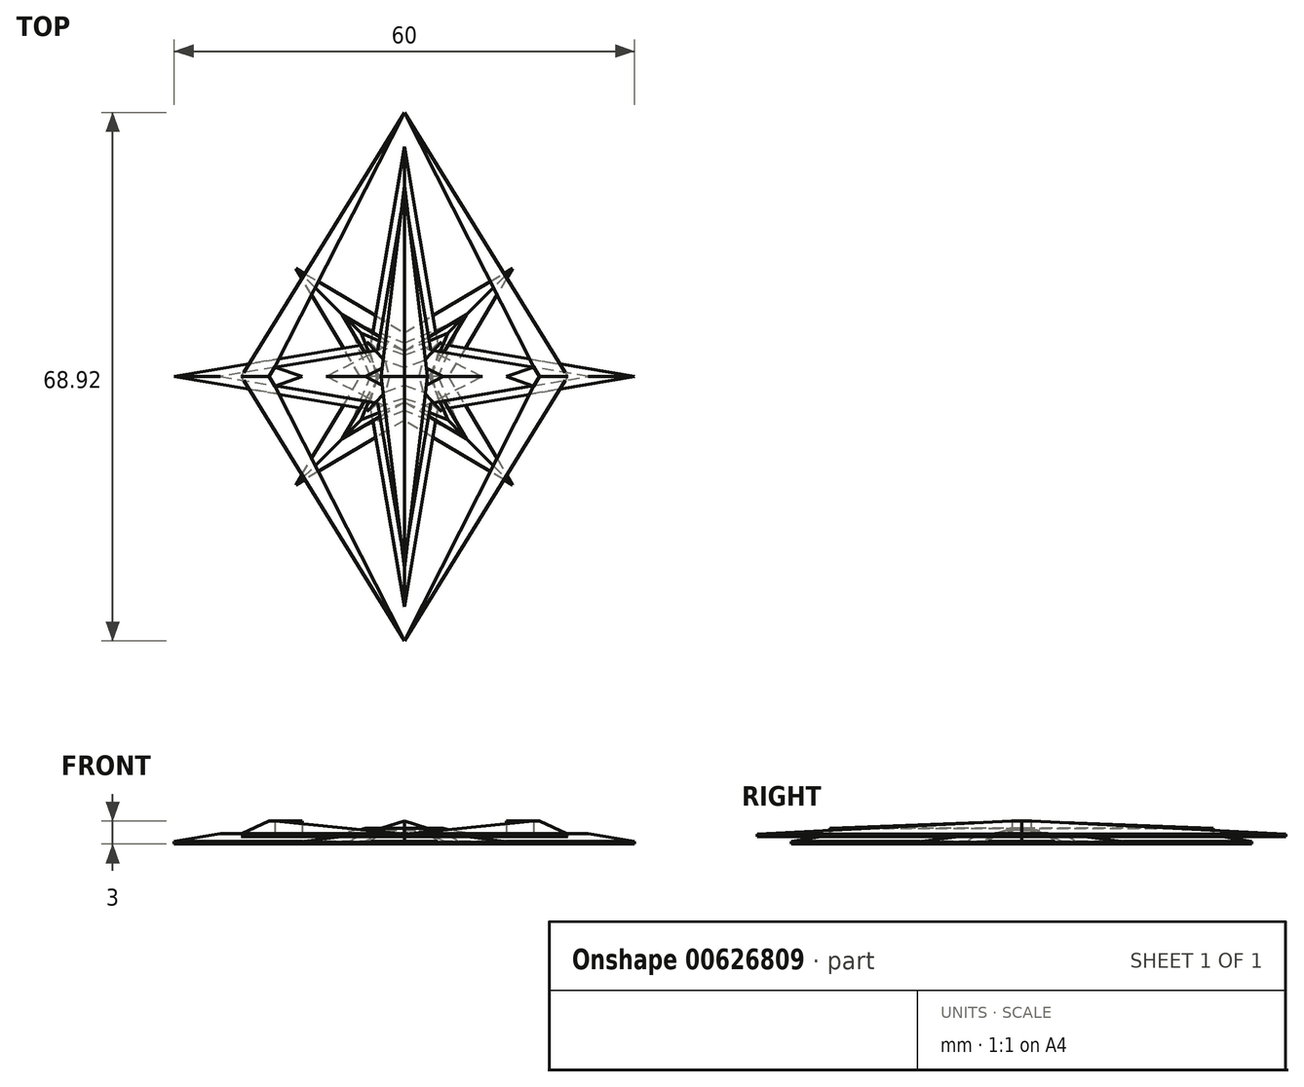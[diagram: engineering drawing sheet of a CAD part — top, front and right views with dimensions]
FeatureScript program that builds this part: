
annotation { "Feature Type Name" : "Feature", "Feature Type Description" : "" }
export const myFeature = defineFeature(function(context is Context, id is Id, definition is map)
    precondition{}
    {
        {
            var Q0;
            Q0=qCreatedBy(makeId("Top.planeOp"),FACE);
            var sketch = newSketch(context, id + "F0", { "sketchPlane" : qUnion([Q0])});
            skLineSegment(sketch, "E0", {"start": v(0, 0) * mm, "end": v(0, 50) * mm});
            skLineSegment(sketch, "E1", {"start": v(0, 25) * mm, "end": v(10.5, 25) * mm});
            skPoint(sketch, "E1.endSnap0", {"position": v(0, 25) * mm});
            skLineSegment(sketch, "E2.MirrorCS", {"start": v(0, 25) * mm, "end": v(-10.5, 25) * mm});
            skLineSegment(sketch, "E3", {"start": v(-10.5, 25) * mm, "end": v(0, 30.33) * mm});
            skLineSegment(sketch, "E4.MirrorCS", {"start": v(-10.5, 25) * mm, "end": v(0, 19.67) * mm});
            skLineSegment(sketch, "E5.MirrorCS", {"start": v(10.5, 25) * mm, "end": v(0, 30.33) * mm});
            skLineSegment(sketch, "E6.MirrorCS", {"start": v(10.5, 25) * mm, "end": v(0, 19.67) * mm});
            skLineSegment(sketch, "E7", {"start": v(0, 50) * mm, "end": v(-3, 25) * mm});
            skLineSegment(sketch, "E8.MirrorCS", {"start": v(0, 50) * mm, "end": v(3, 25) * mm});
            skLineSegment(sketch, "E9.MirrorCS", {"start": v(0, 0) * mm, "end": v(-3, 25) * mm});
            skLineSegment(sketch, "E10.MirrorCS", {"start": v(0, 0) * mm, "end": v(3, 25) * mm});
            skLineSegment(sketch, "E11", {"start": v(5.42, 30.16) * mm, "end": v(0, 28.23) * mm});
            skLineSegment(sketch, "E12.MirrorCS", {"start": v(5.42, 30.16) * mm, "end": v(3.97, 25) * mm});
            skLineSegment(sketch, "E13.MirrorCS", {"start": v(-5.42, 30.16) * mm, "end": v(0, 28.23) * mm});
            skLineSegment(sketch, "E14.MirrorCS", {"start": v(-5.42, 30.16) * mm, "end": v(-3.97, 25) * mm});
            skLineSegment(sketch, "E15.MirrorCS", {"start": v(5.42, 19.84) * mm, "end": v(0, 21.77) * mm});
            skLineSegment(sketch, "E16.MirrorCS", {"start": v(5.42, 19.84) * mm, "end": v(3.97, 25) * mm});
            skLineSegment(sketch, "E17.MirrorCS", {"start": v(-5.42, 19.84) * mm, "end": v(0, 21.77) * mm});
            skLineSegment(sketch, "E18.MirrorCS", {"start": v(-5.42, 19.84) * mm, "end": v(-3.97, 25) * mm});
            skLineSegment(sketch, "E19", {"start": v(0, -9.46) * mm, "end": v(-16.87, 23.77) * mm});
            skLineSegment(sketch, "E20.MirrorCS", {"start": v(0, 59.46) * mm, "end": v(-16.87, 26.23) * mm});
            skLineSegment(sketch, "E21.MirrorCS", {"start": v(0, 59.46) * mm, "end": v(16.87, 26.23) * mm});
            skLineSegment(sketch, "E22.MirrorCS", {"start": v(0, -9.46) * mm, "end": v(16.87, 23.77) * mm});
            skLineSegment(sketch, "E23", {"start": v(0, 59.46) * mm, "end": v(-21.27, 25) * mm});
            skPoint(sketch, "E23.endSnap0", {"position": v(-5.25, 25) * mm});
            skLineSegment(sketch, "E24.MirrorCS", {"start": v(0, -9.46) * mm, "end": v(-21.27, 25) * mm});
            skLineSegment(sketch, "E25.MirrorCS", {"start": v(0, 59.46) * mm, "end": v(21.27, 25) * mm});
            skLineSegment(sketch, "E26.MirrorCS", {"start": v(0, -9.46) * mm, "end": v(21.27, 25) * mm});
            skLineSegment(sketch, "E27", {"start": v(-13.32, 25) * mm, "end": v(-16.87, 26.23) * mm});
            skLineSegment(sketch, "E28.MirrorCS", {"start": v(-13.32, 25) * mm, "end": v(-16.87, 23.77) * mm});
            skLineSegment(sketch, "E29.MirrorCS", {"start": v(13.32, 25) * mm, "end": v(16.87, 26.23) * mm});
            skLineSegment(sketch, "E30.MirrorCS", {"start": v(13.32, 25) * mm, "end": v(16.87, 23.77) * mm});
            skPoint(sketch, "E31.orphan", {"position": v(-17.5, 25) * mm});
            skPoint(sketch, "E32.orphan", {"position": v(17.5, 25) * mm});
            skSolve(sketch);
        }
        {
            var Q0;
            Q0=qCreatedBy(makeId("Top.planeOp"),FACE);
            var sketch = newSketch(context, id + "F1", { "sketchPlane" : qUnion([Q0])});
            skLineSegment(sketch, "E33", {"start": v(0, 0) * mm, "end": v(0, 25) * mm});
            skLineSegment(sketch, "E34", {"start": v(0, 25) * mm, "end": v(0, 55) * mm});
            skLineSegment(sketch, "E35", {"start": v(0, 25) * mm, "end": v(30, 25) * mm});
            skLineSegment(sketch, "E36", {"start": v(0, 25) * mm, "end": v(-30, 25) * mm});
            skLineSegment(sketch, "E37", {"start": v(0, 25) * mm, "end": v(0, -5) * mm});
            skLineSegment(sketch, "E38", {"start": v(0, 55) * mm, "end": v(-4.33, 29.33) * mm});
            skLineSegment(sketch, "E39", {"start": v(-4.33, 29.33) * mm, "end": v(-30, 25) * mm});
            skLineSegment(sketch, "E40.MirrorCS", {"start": v(0, 55) * mm, "end": v(4.33, 29.33) * mm});
            skLineSegment(sketch, "E41.MirrorCS", {"start": v(4.33, 29.33) * mm, "end": v(30, 25) * mm});
            skLineSegment(sketch, "E42.MirrorCS", {"start": v(-4.33, 20.67) * mm, "end": v(-30, 25) * mm});
            skLineSegment(sketch, "E43.MirrorCS", {"start": v(0, -5) * mm, "end": v(-4.33, 20.67) * mm});
            skLineSegment(sketch, "E44.MirrorCS", {"start": v(0, -5) * mm, "end": v(4.33, 20.67) * mm});
            skLineSegment(sketch, "E45.MirrorCS", {"start": v(4.33, 20.67) * mm, "end": v(30, 25) * mm});
            skLineSegment(sketch, "E46", {"start": v(0, 25) * mm, "end": v(-7.48, 32.48) * mm});
            skLineSegment(sketch, "E47.MirrorCS", {"start": v(0, 25) * mm, "end": v(7.48, 32.48) * mm});
            skLineSegment(sketch, "E48.MirrorCS", {"start": v(0, 25) * mm, "end": v(-7.48, 17.52) * mm});
            skLineSegment(sketch, "E49.MirrorCS", {"start": v(0, 25) * mm, "end": v(7.48, 17.52) * mm});
            skLineSegment(sketch, "E50", {"start": v(-7.48, 32.48) * mm, "end": v(-4.41, 25) * mm});
            skLineSegment(sketch, "E51.MirrorCS", {"start": v(-7.48, 32.48) * mm, "end": v(0, 29.41) * mm});
            skLineSegment(sketch, "E52.MirrorCS", {"start": v(7.48, 32.48) * mm, "end": v(0, 29.41) * mm});
            skLineSegment(sketch, "E53.MirrorCS", {"start": v(7.48, 32.48) * mm, "end": v(4.41, 25) * mm});
            skLineSegment(sketch, "E54.MirrorCS", {"start": v(-7.48, 17.52) * mm, "end": v(0, 20.59) * mm});
            skLineSegment(sketch, "E55.MirrorCS", {"start": v(-7.48, 17.52) * mm, "end": v(-4.41, 25) * mm});
            skLineSegment(sketch, "E56.MirrorCS", {"start": v(7.48, 17.52) * mm, "end": v(0, 20.59) * mm});
            skLineSegment(sketch, "E57.MirrorCS", {"start": v(7.48, 17.52) * mm, "end": v(4.41, 25) * mm});
            skSolve(sketch);
        }
        {
            var Q0;
            Q0=qCreatedBy(makeId("Top.planeOp"),FACE);
            var sketch = newSketch(context, id + "F2", { "sketchPlane" : qUnion([Q0])});
            skLineSegment(sketch, "E58", {"start": v(0, 0) * mm, "end": v(0, 25) * mm});
            skLineSegment(sketch, "E59", {"start": v(0, 25) * mm, "end": v(25, 25) * mm});
            skLineSegment(sketch, "E60", {"start": v(0, 25) * mm, "end": v(14.14, 10.86) * mm});
            skLineSegment(sketch, "E61.MirrorCS", {"start": v(0, 25) * mm, "end": v(14.14, 39.14) * mm});
            skLineSegment(sketch, "E62.MirrorCS", {"start": v(0, 25) * mm, "end": v(-14.14, 39.14) * mm});
            skLineSegment(sketch, "E63.MirrorCS", {"start": v(0, 25) * mm, "end": v(-14.14, 10.86) * mm});
            skLineSegment(sketch, "E64", {"start": v(-14.14, 39.14) * mm, "end": v(-5.72, 25) * mm});
            skLineSegment(sketch, "E65", {"start": v(-5.72, 25) * mm, "end": v(-14.14, 10.86) * mm});
            skPoint(sketch, "E66", {"position": v(-5.72, 25) * mm});
            skPoint(sketch, "E67.MirrorP", {"position": v(0, 30.72) * mm});
            skPoint(sketch, "E68.MirrorP", {"position": v(5.72, 25) * mm});
            skPoint(sketch, "E69.MirrorP", {"position": v(0, 19.28) * mm});
            skLineSegment(sketch, "E70", {"start": v(-14.14, 10.86) * mm, "end": v(0, 19.28) * mm});
            skLineSegment(sketch, "E71", {"start": v(14.14, 10.86) * mm, "end": v(0, 19.28) * mm});
            skLineSegment(sketch, "E72", {"start": v(14.14, 10.86) * mm, "end": v(5.72, 25) * mm});
            skLineSegment(sketch, "E73", {"start": v(5.72, 25) * mm, "end": v(14.14, 39.14) * mm});
            skLineSegment(sketch, "E74", {"start": v(14.14, 39.14) * mm, "end": v(0, 30.72) * mm});
            skLineSegment(sketch, "E75", {"start": v(0, 30.72) * mm, "end": v(-14.14, 39.14) * mm});
            skSolve(sketch);
        }
        {
            var Q0;
            {var subQ3=sQuery(id+"F0.wireOp",EDGE,"E3");var subQ5=sQuery(id+"F0.wireOp",EDGE,"E7");var subQ7=makeQuery(id+"F0.imprint","INTERSECT",VERTEX,{"derivedFrom":[subQ3,subQ5]});Q0=makeQuery(id+"F0.imprint","IMPRINT",FACE,{"disambiguationData":[TD([[makeQuery(id+"F0.imprint","IMPRINT",EDGE,{"disambiguationData":[TD([[subQ7,-1.0]])],"derivedFrom":subQ3}),-1.0]])]});}
            var Q1;
            {var subQ3=sQuery(id+"F0.wireOp",EDGE,"E4.MirrorCS");var subQ5=sQuery(id+"F0.wireOp",EDGE,"E9.MirrorCS");var subQ7=makeQuery(id+"F0.imprint","INTERSECT",VERTEX,{"derivedFrom":[subQ3,subQ5]});Q1=makeQuery(id+"F0.imprint","IMPRINT",FACE,{"disambiguationData":[TD([[makeQuery(id+"F0.imprint","IMPRINT",EDGE,{"disambiguationData":[TD([[subQ7,-1.0]])],"derivedFrom":subQ3}),1.0]])]});}
            var Q2;
            {var subQ3=sQuery(id+"F0.wireOp",EDGE,"E5.MirrorCS");var subQ5=sQuery(id+"F0.wireOp",EDGE,"E8.MirrorCS");var subQ7=makeQuery(id+"F0.imprint","INTERSECT",VERTEX,{"derivedFrom":[subQ3,subQ5]});Q2=makeQuery(id+"F0.imprint","IMPRINT",FACE,{"disambiguationData":[TD([[makeQuery(id+"F0.imprint","IMPRINT",EDGE,{"disambiguationData":[TD([[subQ7,-1.0]])],"derivedFrom":subQ3}),1.0]])]});}
            var Q3;
            {var subQ3=sQuery(id+"F0.wireOp",EDGE,"E6.MirrorCS");var subQ5=sQuery(id+"F0.wireOp",EDGE,"E10.MirrorCS");var subQ7=makeQuery(id+"F0.imprint","INTERSECT",VERTEX,{"derivedFrom":[subQ3,subQ5]});Q3=makeQuery(id+"F0.imprint","IMPRINT",FACE,{"disambiguationData":[TD([[makeQuery(id+"F0.imprint","IMPRINT",EDGE,{"disambiguationData":[TD([[subQ7,-1.0]])],"derivedFrom":subQ3}),-1.0]])]});}
            var Q4;
            {var subQ0=sQuery(id+"F0.wireOp",EDGE,"E8.MirrorCS");var subQ5=makeQuery(id+"F0.imprint","INTERSECT",VERTEX,{"derivedFrom":[subQ0,sQuery(id+"F0.wireOp",EDGE,"E11")]});Q4=makeQuery(id+"F0.imprint","IMPRINT",FACE,{"disambiguationData":[TD([[makeQuery(id+"F0.imprint","IMPRINT",EDGE,{"disambiguationData":[TD([[subQ5,-1.0]])],"derivedFrom":subQ0}),-1.0]])]});}
            var Q5;
            {var subQ0=sQuery(id+"F0.wireOp",EDGE,"E7");var subQ6=makeQuery(id+"F0.imprint","INTERSECT",VERTEX,{"derivedFrom":[subQ0,sQuery(id+"F0.wireOp",EDGE,"E13.MirrorCS")]});Q5=makeQuery(id+"F0.imprint","IMPRINT",FACE,{"disambiguationData":[TD([[makeQuery(id+"F0.imprint","IMPRINT",EDGE,{"disambiguationData":[TD([[subQ6,-1.0]])],"derivedFrom":subQ0}),1.0]])]});}
            var Q6;
            {var subQ0=sQuery(id+"F0.wireOp",EDGE,"E9.MirrorCS");var subQ6=makeQuery(id+"F0.imprint","INTERSECT",VERTEX,{"derivedFrom":[subQ0,sQuery(id+"F0.wireOp",EDGE,"E17.MirrorCS")]});Q6=makeQuery(id+"F0.imprint","IMPRINT",FACE,{"disambiguationData":[TD([[makeQuery(id+"F0.imprint","IMPRINT",EDGE,{"disambiguationData":[TD([[subQ6,-1.0]])],"derivedFrom":subQ0}),-1.0]])]});}
            var Q7;
            {var subQ0=sQuery(id+"F0.wireOp",EDGE,"E10.MirrorCS");var subQ5=makeQuery(id+"F0.imprint","INTERSECT",VERTEX,{"derivedFrom":[subQ0,sQuery(id+"F0.wireOp",EDGE,"E15.MirrorCS")]});Q7=makeQuery(id+"F0.imprint","IMPRINT",FACE,{"disambiguationData":[TD([[makeQuery(id+"F0.imprint","IMPRINT",EDGE,{"disambiguationData":[TD([[subQ5,-1.0]])],"derivedFrom":subQ0}),1.0]])]});}
            var Q8;
            {var subQ0=sQuery(id+"F0.wireOp",EDGE,"E4.MirrorCS");var subQ3=sQuery(id+"F0.wireOp",EDGE,"E17.MirrorCS");var subQ5=makeQuery(id+"F0.imprint","INTERSECT",VERTEX,{"derivedFrom":[subQ0,subQ3]});Q8=makeQuery(id+"F0.imprint","IMPRINT",FACE,{"disambiguationData":[TD([[makeQuery(id+"F0.imprint","IMPRINT",EDGE,{"disambiguationData":[TD([[subQ5,-1.0]])],"derivedFrom":subQ0}),1.0]])]});}
            var Q9;
            {var subQ0=sQuery(id+"F0.wireOp",EDGE,"E6.MirrorCS");var subQ3=sQuery(id+"F0.wireOp",EDGE,"E15.MirrorCS");var subQ5=makeQuery(id+"F0.imprint","INTERSECT",VERTEX,{"derivedFrom":[subQ0,subQ3]});Q9=makeQuery(id+"F0.imprint","IMPRINT",FACE,{"disambiguationData":[TD([[makeQuery(id+"F0.imprint","IMPRINT",EDGE,{"disambiguationData":[TD([[subQ5,-1.0]])],"derivedFrom":subQ0}),-1.0]])]});}
            var Q10;
            {var subQ3=sQuery(id+"F0.wireOp",EDGE,"E6.MirrorCS");var subQ5=sQuery(id+"F0.wireOp",EDGE,"E15.MirrorCS");var subQ6=makeQuery(id+"F0.imprint","INTERSECT",VERTEX,{"derivedFrom":[subQ3,subQ5]});Q10=makeQuery(id+"F0.imprint","IMPRINT",FACE,{"disambiguationData":[TD([[makeQuery(id+"F0.imprint","IMPRINT",EDGE,{"disambiguationData":[TD([[subQ6,1.0]])],"derivedFrom":subQ5}),1.0]])]});}
            var Q11;
            {var subQ3=sQuery(id+"F0.wireOp",EDGE,"E4.MirrorCS");var subQ5=sQuery(id+"F0.wireOp",EDGE,"E17.MirrorCS");var subQ6=makeQuery(id+"F0.imprint","INTERSECT",VERTEX,{"derivedFrom":[subQ3,subQ5]});Q11=makeQuery(id+"F0.imprint","IMPRINT",FACE,{"disambiguationData":[TD([[makeQuery(id+"F0.imprint","IMPRINT",EDGE,{"disambiguationData":[TD([[subQ6,1.0]])],"derivedFrom":subQ5}),-1.0]])]});}
            var Q12;
            {var subQ3=sQuery(id+"F0.wireOp",EDGE,"E3");var subQ5=sQuery(id+"F0.wireOp",EDGE,"E13.MirrorCS");var subQ6=makeQuery(id+"F0.imprint","INTERSECT",VERTEX,{"derivedFrom":[subQ3,subQ5]});Q12=makeQuery(id+"F0.imprint","IMPRINT",FACE,{"disambiguationData":[TD([[makeQuery(id+"F0.imprint","IMPRINT",EDGE,{"disambiguationData":[TD([[subQ6,1.0]])],"derivedFrom":subQ5}),1.0]])]});}
            var Q13;
            {var subQ3=sQuery(id+"F0.wireOp",EDGE,"E5.MirrorCS");var subQ5=sQuery(id+"F0.wireOp",EDGE,"E11");var subQ6=makeQuery(id+"F0.imprint","INTERSECT",VERTEX,{"derivedFrom":[subQ3,subQ5]});Q13=makeQuery(id+"F0.imprint","IMPRINT",FACE,{"disambiguationData":[TD([[makeQuery(id+"F0.imprint","IMPRINT",EDGE,{"disambiguationData":[TD([[subQ6,1.0]])],"derivedFrom":subQ5}),-1.0]])]});}
            var Q14;
            {var subQ0=sQuery(id+"F0.wireOp",EDGE,"E5.MirrorCS");var subQ3=sQuery(id+"F0.wireOp",EDGE,"E11");var subQ5=makeQuery(id+"F0.imprint","INTERSECT",VERTEX,{"derivedFrom":[subQ0,subQ3]});Q14=makeQuery(id+"F0.imprint","IMPRINT",FACE,{"disambiguationData":[TD([[makeQuery(id+"F0.imprint","IMPRINT",EDGE,{"disambiguationData":[TD([[subQ5,-1.0]])],"derivedFrom":subQ0}),1.0]])]});}
            var Q15;
            {var subQ0=sQuery(id+"F0.wireOp",EDGE,"E3");var subQ3=sQuery(id+"F0.wireOp",EDGE,"E13.MirrorCS");var subQ5=makeQuery(id+"F0.imprint","INTERSECT",VERTEX,{"derivedFrom":[subQ0,subQ3]});Q15=makeQuery(id+"F0.imprint","IMPRINT",FACE,{"disambiguationData":[TD([[makeQuery(id+"F0.imprint","IMPRINT",EDGE,{"disambiguationData":[TD([[subQ5,-1.0]])],"derivedFrom":subQ0}),-1.0]])]});}
            extrude(context, id + "F3", {"entities" : qUnion([Q0, Q1, Q2, Q3, Q4, Q5, Q6, Q7, Q8, Q9, Q10, Q11, Q12, Q13, Q14, Q15]), "depth" : 2 * mm, "offsetDistance" : 25 * mm});
        }
        {
            var Q0;
            {var subQ0=sQuery(id+"F0.wireOp",EDGE,"E3");var subQ6=makeQuery(id+"F0.imprint","INTERSECT",VERTEX,{"derivedFrom":[subQ0,sQuery(id+"F0.wireOp",EDGE,"E14.MirrorCS")]});Q0=makeQuery(id+"F0.imprint","IMPRINT",FACE,{"disambiguationData":[TD([[makeQuery(id+"F0.imprint","IMPRINT",EDGE,{"disambiguationData":[TD([[subQ6,-1.0]])],"derivedFrom":subQ0}),-1.0]])]});}
            var Q1;
            {var subQ0=sQuery(id+"F0.wireOp",EDGE,"E4.MirrorCS");var subQ5=makeQuery(id+"F0.imprint","INTERSECT",VERTEX,{"derivedFrom":[subQ0,sQuery(id+"F0.wireOp",EDGE,"E18.MirrorCS")]});Q1=makeQuery(id+"F0.imprint","IMPRINT",FACE,{"disambiguationData":[TD([[makeQuery(id+"F0.imprint","IMPRINT",EDGE,{"disambiguationData":[TD([[subQ5,-1.0]])],"derivedFrom":subQ0}),1.0]])]});}
            var Q2;
            {var subQ0=sQuery(id+"F0.wireOp",EDGE,"E5.MirrorCS");var subQ5=makeQuery(id+"F0.imprint","INTERSECT",VERTEX,{"derivedFrom":[subQ0,sQuery(id+"F0.wireOp",EDGE,"E12.MirrorCS")]});Q2=makeQuery(id+"F0.imprint","IMPRINT",FACE,{"disambiguationData":[TD([[makeQuery(id+"F0.imprint","IMPRINT",EDGE,{"disambiguationData":[TD([[subQ5,-1.0]])],"derivedFrom":subQ0}),1.0]])]});}
            var Q3;
            {var subQ0=sQuery(id+"F0.wireOp",EDGE,"E6.MirrorCS");var subQ5=makeQuery(id+"F0.imprint","INTERSECT",VERTEX,{"derivedFrom":[subQ0,sQuery(id+"F0.wireOp",EDGE,"E16.MirrorCS")]});Q3=makeQuery(id+"F0.imprint","IMPRINT",FACE,{"disambiguationData":[TD([[makeQuery(id+"F0.imprint","IMPRINT",EDGE,{"disambiguationData":[TD([[subQ5,-1.0]])],"derivedFrom":subQ0}),-1.0]])]});}
            var Q4;
            {var subQ0=sQuery(id+"F0.wireOp",EDGE,"E3");var subQ3=sQuery(id+"F0.wireOp",EDGE,"E14.MirrorCS");var subQ5=makeQuery(id+"F0.imprint","INTERSECT",VERTEX,{"derivedFrom":[subQ0,subQ3]});Q4=makeQuery(id+"F0.imprint","IMPRINT",FACE,{"disambiguationData":[TD([[makeQuery(id+"F0.imprint","IMPRINT",EDGE,{"disambiguationData":[TD([[subQ5,1.0]])],"derivedFrom":subQ0}),-1.0]])]});}
            var Q5;
            {var subQ0=sQuery(id+"F0.wireOp",EDGE,"E4.MirrorCS");var subQ3=sQuery(id+"F0.wireOp",EDGE,"E18.MirrorCS");var subQ5=makeQuery(id+"F0.imprint","INTERSECT",VERTEX,{"derivedFrom":[subQ0,subQ3]});Q5=makeQuery(id+"F0.imprint","IMPRINT",FACE,{"disambiguationData":[TD([[makeQuery(id+"F0.imprint","IMPRINT",EDGE,{"disambiguationData":[TD([[subQ5,1.0]])],"derivedFrom":subQ0}),1.0]])]});}
            var Q6;
            {var subQ0=sQuery(id+"F0.wireOp",EDGE,"E5.MirrorCS");var subQ3=sQuery(id+"F0.wireOp",EDGE,"E12.MirrorCS");var subQ5=makeQuery(id+"F0.imprint","INTERSECT",VERTEX,{"derivedFrom":[subQ0,subQ3]});Q6=makeQuery(id+"F0.imprint","IMPRINT",FACE,{"disambiguationData":[TD([[makeQuery(id+"F0.imprint","IMPRINT",EDGE,{"disambiguationData":[TD([[subQ5,1.0]])],"derivedFrom":subQ0}),1.0]])]});}
            var Q7;
            {var subQ0=sQuery(id+"F0.wireOp",EDGE,"E6.MirrorCS");var subQ3=sQuery(id+"F0.wireOp",EDGE,"E16.MirrorCS");var subQ5=makeQuery(id+"F0.imprint","INTERSECT",VERTEX,{"derivedFrom":[subQ0,subQ3]});Q7=makeQuery(id+"F0.imprint","IMPRINT",FACE,{"disambiguationData":[TD([[makeQuery(id+"F0.imprint","IMPRINT",EDGE,{"disambiguationData":[TD([[subQ5,1.0]])],"derivedFrom":subQ0}),-1.0]])]});}
            extrude(context, id + "F4", {"entities" : qUnion([Q0, Q1, Q2, Q3, Q4, Q5, Q6, Q7]), "operationType" : NewBodyOperationType.ADD, "depth" : 1.03 * mm, "offsetDistance" : 25 * mm});
        }
        {
            var Q0;
            {var subQ0=sQuery(id+"F0.wireOp",EDGE,"E14.MirrorCS");var subQ1=sQuery(id+"F0.wireOp",EDGE,"E3");var subQ2=makeQuery(id+"F0.imprint","INTERSECT",VERTEX,{"derivedFrom":[subQ1,subQ0]});Q0=makeQuery(id+"F0.imprint","IMPRINT",FACE,{"disambiguationData":[TD([[makeQuery(id+"F0.imprint","IMPRINT",EDGE,{"disambiguationData":[TD([[subQ2,-1.0]])],"derivedFrom":subQ1}),1.0]])]});}
            var Q1;
            {var subQ3=sQuery(id+"F0.wireOp",EDGE,"E14.MirrorCS");var subQ5=sQuery(id+"F0.wireOp",EDGE,"E3");var subQ7=makeQuery(id+"F0.imprint","INTERSECT",VERTEX,{"derivedFrom":[subQ5,subQ3]});Q1=makeQuery(id+"F0.imprint","IMPRINT",FACE,{"disambiguationData":[TD([[makeQuery(id+"F0.imprint","IMPRINT",EDGE,{"disambiguationData":[TD([[subQ7,-1.0]])],"derivedFrom":subQ5}),-1.0]])]});}
            var Q2;
            {var subQ3=sQuery(id+"F0.wireOp",EDGE,"E12.MirrorCS");var subQ5=sQuery(id+"F0.wireOp",EDGE,"E5.MirrorCS");var subQ6=makeQuery(id+"F0.imprint","INTERSECT",VERTEX,{"derivedFrom":[subQ5,subQ3]});Q2=makeQuery(id+"F0.imprint","IMPRINT",FACE,{"disambiguationData":[TD([[makeQuery(id+"F0.imprint","IMPRINT",EDGE,{"disambiguationData":[TD([[subQ6,-1.0]])],"derivedFrom":subQ5}),1.0]])]});}
            var Q3;
            {var subQ0=sQuery(id+"F0.wireOp",EDGE,"E12.MirrorCS");var subQ1=sQuery(id+"F0.wireOp",EDGE,"E5.MirrorCS");var subQ2=makeQuery(id+"F0.imprint","INTERSECT",VERTEX,{"derivedFrom":[subQ1,subQ0]});Q3=makeQuery(id+"F0.imprint","IMPRINT",FACE,{"disambiguationData":[TD([[makeQuery(id+"F0.imprint","IMPRINT",EDGE,{"disambiguationData":[TD([[subQ2,-1.0]])],"derivedFrom":subQ1}),-1.0]])]});}
            var Q4;
            {var subQ3=sQuery(id+"F0.wireOp",EDGE,"E16.MirrorCS");var subQ5=sQuery(id+"F0.wireOp",EDGE,"E6.MirrorCS");var subQ6=makeQuery(id+"F0.imprint","INTERSECT",VERTEX,{"derivedFrom":[subQ5,subQ3]});Q4=makeQuery(id+"F0.imprint","IMPRINT",FACE,{"disambiguationData":[TD([[makeQuery(id+"F0.imprint","IMPRINT",EDGE,{"disambiguationData":[TD([[subQ6,-1.0]])],"derivedFrom":subQ5}),-1.0]])]});}
            var Q5;
            {var subQ0=sQuery(id+"F0.wireOp",EDGE,"E16.MirrorCS");var subQ1=sQuery(id+"F0.wireOp",EDGE,"E6.MirrorCS");var subQ2=makeQuery(id+"F0.imprint","INTERSECT",VERTEX,{"derivedFrom":[subQ1,subQ0]});Q5=makeQuery(id+"F0.imprint","IMPRINT",FACE,{"disambiguationData":[TD([[makeQuery(id+"F0.imprint","IMPRINT",EDGE,{"disambiguationData":[TD([[subQ2,-1.0]])],"derivedFrom":subQ1}),1.0]])]});}
            var Q6;
            {var subQ3=sQuery(id+"F0.wireOp",EDGE,"E18.MirrorCS");var subQ5=sQuery(id+"F0.wireOp",EDGE,"E4.MirrorCS");var subQ6=makeQuery(id+"F0.imprint","INTERSECT",VERTEX,{"derivedFrom":[subQ5,subQ3]});Q6=makeQuery(id+"F0.imprint","IMPRINT",FACE,{"disambiguationData":[TD([[makeQuery(id+"F0.imprint","IMPRINT",EDGE,{"disambiguationData":[TD([[subQ6,-1.0]])],"derivedFrom":subQ5}),1.0]])]});}
            var Q7;
            {var subQ0=sQuery(id+"F0.wireOp",EDGE,"E18.MirrorCS");var subQ1=sQuery(id+"F0.wireOp",EDGE,"E4.MirrorCS");var subQ2=makeQuery(id+"F0.imprint","INTERSECT",VERTEX,{"derivedFrom":[subQ1,subQ0]});Q7=makeQuery(id+"F0.imprint","IMPRINT",FACE,{"disambiguationData":[TD([[makeQuery(id+"F0.imprint","IMPRINT",EDGE,{"disambiguationData":[TD([[subQ2,-1.0]])],"derivedFrom":subQ1}),-1.0]])]});}
            var Q8;
            {var subQ0=sQuery(id+"F0.wireOp",EDGE,"E9.MirrorCS");var subQ3=sQuery(id+"F0.wireOp",EDGE,"E4.MirrorCS");var subQ4=makeQuery(id+"F0.imprint","INTERSECT",VERTEX,{"derivedFrom":[subQ3,subQ0]});Q8=makeQuery(id+"F0.imprint","IMPRINT",FACE,{"disambiguationData":[TD([[makeQuery(id+"F0.imprint","IMPRINT",EDGE,{"disambiguationData":[TD([[subQ4,-1.0]])],"derivedFrom":subQ3}),1.0]])]});}
            var Q9;
            {var subQ0=sQuery(id+"F0.wireOp",EDGE,"E7");var subQ3=sQuery(id+"F0.wireOp",EDGE,"E3");var subQ4=makeQuery(id+"F0.imprint","INTERSECT",VERTEX,{"derivedFrom":[subQ3,subQ0]});Q9=makeQuery(id+"F0.imprint","IMPRINT",FACE,{"disambiguationData":[TD([[makeQuery(id+"F0.imprint","IMPRINT",EDGE,{"disambiguationData":[TD([[subQ4,-1.0]])],"derivedFrom":subQ3}),-1.0]])]});}
            var Q10;
            {var subQ0=sQuery(id+"F0.wireOp",EDGE,"E8.MirrorCS");var subQ1=sQuery(id+"F0.wireOp",EDGE,"E5.MirrorCS");var subQ2=makeQuery(id+"F0.imprint","INTERSECT",VERTEX,{"derivedFrom":[subQ1,subQ0]});Q10=makeQuery(id+"F0.imprint","IMPRINT",FACE,{"disambiguationData":[TD([[makeQuery(id+"F0.imprint","IMPRINT",EDGE,{"disambiguationData":[TD([[subQ2,-1.0]])],"derivedFrom":subQ1}),1.0]])]});}
            var Q11;
            {var subQ0=sQuery(id+"F0.wireOp",EDGE,"E10.MirrorCS");var subQ3=sQuery(id+"F0.wireOp",EDGE,"E6.MirrorCS");var subQ4=makeQuery(id+"F0.imprint","INTERSECT",VERTEX,{"derivedFrom":[subQ3,subQ0]});Q11=makeQuery(id+"F0.imprint","IMPRINT",FACE,{"disambiguationData":[TD([[makeQuery(id+"F0.imprint","IMPRINT",EDGE,{"disambiguationData":[TD([[subQ4,-1.0]])],"derivedFrom":subQ3}),-1.0]])]});}
            var Q12;
            {var subQ0=sQuery(id+"F0.wireOp",EDGE,"E9.MirrorCS");var subQ1=sQuery(id+"F0.wireOp",EDGE,"E4.MirrorCS");var subQ2=makeQuery(id+"F0.imprint","INTERSECT",VERTEX,{"derivedFrom":[subQ1,subQ0]});Q12=makeQuery(id+"F0.imprint","IMPRINT",FACE,{"disambiguationData":[TD([[makeQuery(id+"F0.imprint","IMPRINT",EDGE,{"disambiguationData":[TD([[subQ2,-1.0]])],"derivedFrom":subQ1}),-1.0]])]});}
            var Q13;
            {var subQ0=sQuery(id+"F0.wireOp",EDGE,"E10.MirrorCS");var subQ1=sQuery(id+"F0.wireOp",EDGE,"E6.MirrorCS");var subQ2=makeQuery(id+"F0.imprint","INTERSECT",VERTEX,{"derivedFrom":[subQ1,subQ0]});Q13=makeQuery(id+"F0.imprint","IMPRINT",FACE,{"disambiguationData":[TD([[makeQuery(id+"F0.imprint","IMPRINT",EDGE,{"disambiguationData":[TD([[subQ2,-1.0]])],"derivedFrom":subQ1}),1.0]])]});}
            var Q14;
            {var subQ0=sQuery(id+"F0.wireOp",EDGE,"E8.MirrorCS");var subQ1=sQuery(id+"F0.wireOp",EDGE,"E5.MirrorCS");var subQ2=makeQuery(id+"F0.imprint","INTERSECT",VERTEX,{"derivedFrom":[subQ1,subQ0]});Q14=makeQuery(id+"F0.imprint","IMPRINT",FACE,{"disambiguationData":[TD([[makeQuery(id+"F0.imprint","IMPRINT",EDGE,{"disambiguationData":[TD([[subQ2,-1.0]])],"derivedFrom":subQ1}),-1.0]])]});}
            var Q15;
            {var subQ0=sQuery(id+"F0.wireOp",EDGE,"E7");var subQ1=sQuery(id+"F0.wireOp",EDGE,"E3");var subQ2=makeQuery(id+"F0.imprint","INTERSECT",VERTEX,{"derivedFrom":[subQ1,subQ0]});Q15=makeQuery(id+"F0.imprint","IMPRINT",FACE,{"disambiguationData":[TD([[makeQuery(id+"F0.imprint","IMPRINT",EDGE,{"disambiguationData":[TD([[subQ2,-1.0]])],"derivedFrom":subQ1}),1.0]])]});}
            extrude(context, id + "F5", {"entities" : qUnion([Q0, Q1, Q2, Q3, Q4, Q5, Q6, Q7, Q8, Q9, Q10, Q11, Q12, Q13, Q14, Q15]), "depth" : 0.8 * mm, "offsetDistance" : 25 * mm});
        }
        {
            var Q0;
            Q0=makeQuery(id+"F0.imprint","IMPRINT",FACE,{"disambiguationData":[TD([[makeQuery(id+"F0.imprint","IMPRINT",EDGE,{"derivedFrom":sQuery(id+"F0.wireOp",EDGE,"E19")}),1.0]])]});
            var Q1;
            Q1=makeQuery(id+"F0.imprint","IMPRINT",FACE,{"disambiguationData":[TD([[makeQuery(id+"F0.imprint","IMPRINT",EDGE,{"derivedFrom":sQuery(id+"F0.wireOp",EDGE,"E22.MirrorCS")}),-1.0]])]});
            extrude(context, id + "F6", {"entities" : qUnion([Q0, Q1]), "depth" : 2 * mm, "offsetDistance" : 25 * mm});
        }
        {
            var Q0;
            {var subQ0=sQuery(id+"F1.wireOp",EDGE,"E55.MirrorCS");var subQ3=sQuery(id+"F1.wireOp",EDGE,"E42.MirrorCS");var subQ5=makeQuery(id+"F1.imprint","INTERSECT",VERTEX,{"derivedFrom":[subQ3,subQ0]});Q0=makeQuery(id+"F1.imprint","IMPRINT",FACE,{"disambiguationData":[TD([[makeQuery(id+"F1.imprint","IMPRINT",EDGE,{"disambiguationData":[TD([[subQ5,-1.0]])],"derivedFrom":subQ3}),-1.0]])]});}
            var Q1;
            {var subQ0=sQuery(id+"F1.wireOp",EDGE,"E50");var subQ3=sQuery(id+"F1.wireOp",EDGE,"E39");var subQ5=makeQuery(id+"F1.imprint","INTERSECT",VERTEX,{"derivedFrom":[subQ3,subQ0]});Q1=makeQuery(id+"F1.imprint","IMPRINT",FACE,{"disambiguationData":[TD([[makeQuery(id+"F1.imprint","IMPRINT",EDGE,{"disambiguationData":[TD([[subQ5,-1.0]])],"derivedFrom":subQ3}),1.0]])]});}
            var Q2;
            {var subQ0=sQuery(id+"F1.wireOp",EDGE,"E53.MirrorCS");var subQ3=sQuery(id+"F1.wireOp",EDGE,"E41.MirrorCS");var subQ5=makeQuery(id+"F1.imprint","INTERSECT",VERTEX,{"derivedFrom":[subQ3,subQ0]});Q2=makeQuery(id+"F1.imprint","IMPRINT",FACE,{"disambiguationData":[TD([[makeQuery(id+"F1.imprint","IMPRINT",EDGE,{"disambiguationData":[TD([[subQ5,-1.0]])],"derivedFrom":subQ3}),-1.0]])]});}
            var Q3;
            {var subQ0=sQuery(id+"F1.wireOp",EDGE,"E57.MirrorCS");var subQ3=sQuery(id+"F1.wireOp",EDGE,"E45.MirrorCS");var subQ5=makeQuery(id+"F1.imprint","INTERSECT",VERTEX,{"derivedFrom":[subQ3,subQ0]});Q3=makeQuery(id+"F1.imprint","IMPRINT",FACE,{"disambiguationData":[TD([[makeQuery(id+"F1.imprint","IMPRINT",EDGE,{"disambiguationData":[TD([[subQ5,-1.0]])],"derivedFrom":subQ3}),1.0]])]});}
            var Q4;
            {var subQ0=sQuery(id+"F1.wireOp",EDGE,"E52.MirrorCS");var subQ3=sQuery(id+"F1.wireOp",EDGE,"E40.MirrorCS");var subQ5=makeQuery(id+"F1.imprint","INTERSECT",VERTEX,{"derivedFrom":[subQ3,subQ0]});Q4=makeQuery(id+"F1.imprint","IMPRINT",FACE,{"disambiguationData":[TD([[makeQuery(id+"F1.imprint","IMPRINT",EDGE,{"disambiguationData":[TD([[subQ5,1.0]])],"derivedFrom":subQ3}),-1.0]])]});}
            var Q5;
            {var subQ0=sQuery(id+"F1.wireOp",EDGE,"E51.MirrorCS");var subQ3=sQuery(id+"F1.wireOp",EDGE,"E38");var subQ5=makeQuery(id+"F1.imprint","INTERSECT",VERTEX,{"derivedFrom":[subQ3,subQ0]});Q5=makeQuery(id+"F1.imprint","IMPRINT",FACE,{"disambiguationData":[TD([[makeQuery(id+"F1.imprint","IMPRINT",EDGE,{"disambiguationData":[TD([[subQ5,1.0]])],"derivedFrom":subQ3}),1.0]])]});}
            var Q6;
            {var subQ0=sQuery(id+"F1.wireOp",EDGE,"E37");Q6=makeQuery(id+"F1.imprint","IMPRINT",FACE,{"disambiguationData":[TD([[makeQuery(id+"F1.imprint","IMPRINT",EDGE,{"derivedFrom":subQ0}),-1.0]])]});}
            var Q7;
            {var subQ0=sQuery(id+"F1.wireOp",EDGE,"E37");Q7=makeQuery(id+"F1.imprint","IMPRINT",FACE,{"disambiguationData":[TD([[makeQuery(id+"F1.imprint","IMPRINT",EDGE,{"derivedFrom":subQ0}),1.0]])]});}
            var Q8;
            {var subQ3=sQuery(id+"F1.wireOp",EDGE,"E50");var subQ5=sQuery(id+"F1.wireOp",EDGE,"E39");var subQ7=makeQuery(id+"F1.imprint","INTERSECT",VERTEX,{"derivedFrom":[subQ5,subQ3]});Q8=makeQuery(id+"F1.imprint","IMPRINT",FACE,{"disambiguationData":[TD([[makeQuery(id+"F1.imprint","IMPRINT",EDGE,{"disambiguationData":[TD([[subQ7,1.0]])],"derivedFrom":subQ5}),1.0]])]});}
            var Q9;
            {var subQ3=sQuery(id+"F1.wireOp",EDGE,"E55.MirrorCS");var subQ5=sQuery(id+"F1.wireOp",EDGE,"E42.MirrorCS");var subQ6=makeQuery(id+"F1.imprint","INTERSECT",VERTEX,{"derivedFrom":[subQ5,subQ3]});Q9=makeQuery(id+"F1.imprint","IMPRINT",FACE,{"disambiguationData":[TD([[makeQuery(id+"F1.imprint","IMPRINT",EDGE,{"disambiguationData":[TD([[subQ6,1.0]])],"derivedFrom":subQ5}),-1.0]])]});}
            var Q10;
            {var subQ3=sQuery(id+"F1.wireOp",EDGE,"E54.MirrorCS");var subQ5=sQuery(id+"F1.wireOp",EDGE,"E43.MirrorCS");var subQ6=makeQuery(id+"F1.imprint","INTERSECT",VERTEX,{"derivedFrom":[subQ5,subQ3]});Q10=makeQuery(id+"F1.imprint","IMPRINT",FACE,{"disambiguationData":[TD([[makeQuery(id+"F1.imprint","IMPRINT",EDGE,{"disambiguationData":[TD([[subQ6,-1.0]])],"derivedFrom":subQ5}),-1.0]])]});}
            var Q11;
            {var subQ3=sQuery(id+"F1.wireOp",EDGE,"E56.MirrorCS");var subQ5=sQuery(id+"F1.wireOp",EDGE,"E44.MirrorCS");var subQ7=makeQuery(id+"F1.imprint","INTERSECT",VERTEX,{"derivedFrom":[subQ5,subQ3]});Q11=makeQuery(id+"F1.imprint","IMPRINT",FACE,{"disambiguationData":[TD([[makeQuery(id+"F1.imprint","IMPRINT",EDGE,{"disambiguationData":[TD([[subQ7,-1.0]])],"derivedFrom":subQ5}),1.0]])]});}
            var Q12;
            {var subQ3=sQuery(id+"F1.wireOp",EDGE,"E57.MirrorCS");var subQ5=sQuery(id+"F1.wireOp",EDGE,"E45.MirrorCS");var subQ7=makeQuery(id+"F1.imprint","INTERSECT",VERTEX,{"derivedFrom":[subQ5,subQ3]});Q12=makeQuery(id+"F1.imprint","IMPRINT",FACE,{"disambiguationData":[TD([[makeQuery(id+"F1.imprint","IMPRINT",EDGE,{"disambiguationData":[TD([[subQ7,1.0]])],"derivedFrom":subQ5}),1.0]])]});}
            var Q13;
            {var subQ3=sQuery(id+"F1.wireOp",EDGE,"E53.MirrorCS");var subQ5=sQuery(id+"F1.wireOp",EDGE,"E41.MirrorCS");var subQ7=makeQuery(id+"F1.imprint","INTERSECT",VERTEX,{"derivedFrom":[subQ5,subQ3]});Q13=makeQuery(id+"F1.imprint","IMPRINT",FACE,{"disambiguationData":[TD([[makeQuery(id+"F1.imprint","IMPRINT",EDGE,{"disambiguationData":[TD([[subQ7,1.0]])],"derivedFrom":subQ5}),-1.0]])]});}
            var Q14;
            {var subQ3=sQuery(id+"F1.wireOp",EDGE,"E52.MirrorCS");var subQ5=sQuery(id+"F1.wireOp",EDGE,"E40.MirrorCS");var subQ7=makeQuery(id+"F1.imprint","INTERSECT",VERTEX,{"derivedFrom":[subQ5,subQ3]});Q14=makeQuery(id+"F1.imprint","IMPRINT",FACE,{"disambiguationData":[TD([[makeQuery(id+"F1.imprint","IMPRINT",EDGE,{"disambiguationData":[TD([[subQ7,-1.0]])],"derivedFrom":subQ5}),-1.0]])]});}
            var Q15;
            {var subQ3=sQuery(id+"F1.wireOp",EDGE,"E51.MirrorCS");var subQ5=sQuery(id+"F1.wireOp",EDGE,"E38");var subQ7=makeQuery(id+"F1.imprint","INTERSECT",VERTEX,{"derivedFrom":[subQ5,subQ3]});Q15=makeQuery(id+"F1.imprint","IMPRINT",FACE,{"disambiguationData":[TD([[makeQuery(id+"F1.imprint","IMPRINT",EDGE,{"disambiguationData":[TD([[subQ7,-1.0]])],"derivedFrom":subQ5}),1.0]])]});}
            extrude(context, id + "F7", {"entities" : qUnion([Q0, Q1, Q2, Q3, Q4, Q5, Q6, Q7, Q8, Q9, Q10, Q11, Q12, Q13, Q14, Q15]), "depth" : 0.35 * mm, "offsetDistance" : 25 * mm, "hasSecondDirection" : true, "secondDirectionOppositeDirection" : true, "secondDirectionDepth" : 1 * mm});
        }
        {
            var Q0;
            {var subQ1=sQuery(id+"F1.wireOp",EDGE,"E39");var subQ3=sQuery(id+"F1.wireOp",EDGE,"E50");var subQ4=makeQuery(id+"F1.imprint","INTERSECT",VERTEX,{"derivedFrom":[subQ1,subQ3]});Q0=makeQuery(id+"F1.imprint","IMPRINT",FACE,{"disambiguationData":[TD([[makeQuery(id+"F1.imprint","IMPRINT",EDGE,{"disambiguationData":[TD([[subQ4,1.0]])],"derivedFrom":subQ1}),-1.0]])]});}
            var Q1;
            {var subQ1=sQuery(id+"F1.wireOp",EDGE,"E38");var subQ3=sQuery(id+"F1.wireOp",EDGE,"E51.MirrorCS");var subQ4=makeQuery(id+"F1.imprint","INTERSECT",VERTEX,{"derivedFrom":[subQ1,subQ3]});Q1=makeQuery(id+"F1.imprint","IMPRINT",FACE,{"disambiguationData":[TD([[makeQuery(id+"F1.imprint","IMPRINT",EDGE,{"disambiguationData":[TD([[subQ4,-1.0]])],"derivedFrom":subQ1}),-1.0]])]});}
            var Q2;
            {var subQ1=sQuery(id+"F1.wireOp",EDGE,"E41.MirrorCS");var subQ3=sQuery(id+"F1.wireOp",EDGE,"E53.MirrorCS");var subQ4=makeQuery(id+"F1.imprint","INTERSECT",VERTEX,{"derivedFrom":[subQ1,subQ3]});Q2=makeQuery(id+"F1.imprint","IMPRINT",FACE,{"disambiguationData":[TD([[makeQuery(id+"F1.imprint","IMPRINT",EDGE,{"disambiguationData":[TD([[subQ4,1.0]])],"derivedFrom":subQ1}),1.0]])]});}
            var Q3;
            {var subQ1=sQuery(id+"F1.wireOp",EDGE,"E40.MirrorCS");var subQ3=sQuery(id+"F1.wireOp",EDGE,"E52.MirrorCS");var subQ4=makeQuery(id+"F1.imprint","INTERSECT",VERTEX,{"derivedFrom":[subQ1,subQ3]});Q3=makeQuery(id+"F1.imprint","IMPRINT",FACE,{"disambiguationData":[TD([[makeQuery(id+"F1.imprint","IMPRINT",EDGE,{"disambiguationData":[TD([[subQ4,-1.0]])],"derivedFrom":subQ1}),1.0]])]});}
            var Q4;
            {var subQ1=sQuery(id+"F1.wireOp",EDGE,"E44.MirrorCS");var subQ3=sQuery(id+"F1.wireOp",EDGE,"E56.MirrorCS");var subQ4=makeQuery(id+"F1.imprint","INTERSECT",VERTEX,{"derivedFrom":[subQ1,subQ3]});Q4=makeQuery(id+"F1.imprint","IMPRINT",FACE,{"disambiguationData":[TD([[makeQuery(id+"F1.imprint","IMPRINT",EDGE,{"disambiguationData":[TD([[subQ4,-1.0]])],"derivedFrom":subQ1}),-1.0]])]});}
            var Q5;
            {var subQ1=sQuery(id+"F1.wireOp",EDGE,"E45.MirrorCS");var subQ3=sQuery(id+"F1.wireOp",EDGE,"E57.MirrorCS");var subQ4=makeQuery(id+"F1.imprint","INTERSECT",VERTEX,{"derivedFrom":[subQ1,subQ3]});Q5=makeQuery(id+"F1.imprint","IMPRINT",FACE,{"disambiguationData":[TD([[makeQuery(id+"F1.imprint","IMPRINT",EDGE,{"disambiguationData":[TD([[subQ4,1.0]])],"derivedFrom":subQ1}),-1.0]])]});}
            var Q6;
            {var subQ0=sQuery(id+"F1.wireOp",EDGE,"E55.MirrorCS");var subQ1=sQuery(id+"F1.wireOp",EDGE,"E42.MirrorCS");var subQ2=makeQuery(id+"F1.imprint","INTERSECT",VERTEX,{"derivedFrom":[subQ1,subQ0]});Q6=makeQuery(id+"F1.imprint","IMPRINT",FACE,{"disambiguationData":[TD([[makeQuery(id+"F1.imprint","IMPRINT",EDGE,{"disambiguationData":[TD([[subQ2,1.0]])],"derivedFrom":subQ1}),1.0]])]});}
            var Q7;
            {var subQ1=sQuery(id+"F1.wireOp",EDGE,"E43.MirrorCS");var subQ3=sQuery(id+"F1.wireOp",EDGE,"E54.MirrorCS");var subQ4=makeQuery(id+"F1.imprint","INTERSECT",VERTEX,{"derivedFrom":[subQ1,subQ3]});Q7=makeQuery(id+"F1.imprint","IMPRINT",FACE,{"disambiguationData":[TD([[makeQuery(id+"F1.imprint","IMPRINT",EDGE,{"disambiguationData":[TD([[subQ4,-1.0]])],"derivedFrom":subQ1}),1.0]])]});}
            var Q8;
            {var subQ3=sQuery(id+"F1.wireOp",EDGE,"E50");var subQ5=sQuery(id+"F1.wireOp",EDGE,"E39");var subQ7=makeQuery(id+"F1.imprint","INTERSECT",VERTEX,{"derivedFrom":[subQ5,subQ3]});Q8=makeQuery(id+"F1.imprint","IMPRINT",FACE,{"disambiguationData":[TD([[makeQuery(id+"F1.imprint","IMPRINT",EDGE,{"disambiguationData":[TD([[subQ7,1.0]])],"derivedFrom":subQ5}),1.0]])]});}
            var Q9;
            {var subQ3=sQuery(id+"F1.wireOp",EDGE,"E51.MirrorCS");var subQ5=sQuery(id+"F1.wireOp",EDGE,"E38");var subQ7=makeQuery(id+"F1.imprint","INTERSECT",VERTEX,{"derivedFrom":[subQ5,subQ3]});Q9=makeQuery(id+"F1.imprint","IMPRINT",FACE,{"disambiguationData":[TD([[makeQuery(id+"F1.imprint","IMPRINT",EDGE,{"disambiguationData":[TD([[subQ7,-1.0]])],"derivedFrom":subQ5}),1.0]])]});}
            var Q10;
            {var subQ3=sQuery(id+"F1.wireOp",EDGE,"E52.MirrorCS");var subQ5=sQuery(id+"F1.wireOp",EDGE,"E40.MirrorCS");var subQ7=makeQuery(id+"F1.imprint","INTERSECT",VERTEX,{"derivedFrom":[subQ5,subQ3]});Q10=makeQuery(id+"F1.imprint","IMPRINT",FACE,{"disambiguationData":[TD([[makeQuery(id+"F1.imprint","IMPRINT",EDGE,{"disambiguationData":[TD([[subQ7,-1.0]])],"derivedFrom":subQ5}),-1.0]])]});}
            var Q11;
            {var subQ3=sQuery(id+"F1.wireOp",EDGE,"E53.MirrorCS");var subQ5=sQuery(id+"F1.wireOp",EDGE,"E41.MirrorCS");var subQ7=makeQuery(id+"F1.imprint","INTERSECT",VERTEX,{"derivedFrom":[subQ5,subQ3]});Q11=makeQuery(id+"F1.imprint","IMPRINT",FACE,{"disambiguationData":[TD([[makeQuery(id+"F1.imprint","IMPRINT",EDGE,{"disambiguationData":[TD([[subQ7,1.0]])],"derivedFrom":subQ5}),-1.0]])]});}
            var Q12;
            {var subQ3=sQuery(id+"F1.wireOp",EDGE,"E56.MirrorCS");var subQ5=sQuery(id+"F1.wireOp",EDGE,"E44.MirrorCS");var subQ7=makeQuery(id+"F1.imprint","INTERSECT",VERTEX,{"derivedFrom":[subQ5,subQ3]});Q12=makeQuery(id+"F1.imprint","IMPRINT",FACE,{"disambiguationData":[TD([[makeQuery(id+"F1.imprint","IMPRINT",EDGE,{"disambiguationData":[TD([[subQ7,-1.0]])],"derivedFrom":subQ5}),1.0]])]});}
            var Q13;
            {var subQ3=sQuery(id+"F1.wireOp",EDGE,"E57.MirrorCS");var subQ5=sQuery(id+"F1.wireOp",EDGE,"E45.MirrorCS");var subQ7=makeQuery(id+"F1.imprint","INTERSECT",VERTEX,{"derivedFrom":[subQ5,subQ3]});Q13=makeQuery(id+"F1.imprint","IMPRINT",FACE,{"disambiguationData":[TD([[makeQuery(id+"F1.imprint","IMPRINT",EDGE,{"disambiguationData":[TD([[subQ7,1.0]])],"derivedFrom":subQ5}),1.0]])]});}
            var Q14;
            {var subQ3=sQuery(id+"F1.wireOp",EDGE,"E55.MirrorCS");var subQ5=sQuery(id+"F1.wireOp",EDGE,"E42.MirrorCS");var subQ6=makeQuery(id+"F1.imprint","INTERSECT",VERTEX,{"derivedFrom":[subQ5,subQ3]});Q14=makeQuery(id+"F1.imprint","IMPRINT",FACE,{"disambiguationData":[TD([[makeQuery(id+"F1.imprint","IMPRINT",EDGE,{"disambiguationData":[TD([[subQ6,1.0]])],"derivedFrom":subQ5}),-1.0]])]});}
            var Q15;
            {var subQ3=sQuery(id+"F1.wireOp",EDGE,"E54.MirrorCS");var subQ5=sQuery(id+"F1.wireOp",EDGE,"E43.MirrorCS");var subQ6=makeQuery(id+"F1.imprint","INTERSECT",VERTEX,{"derivedFrom":[subQ5,subQ3]});Q15=makeQuery(id+"F1.imprint","IMPRINT",FACE,{"disambiguationData":[TD([[makeQuery(id+"F1.imprint","IMPRINT",EDGE,{"disambiguationData":[TD([[subQ6,-1.0]])],"derivedFrom":subQ5}),-1.0]])]});}
            extrude(context, id + "F8", {"entities" : qUnion([Q0, Q1, Q2, Q3, Q4, Q5, Q6, Q7, Q8, Q9, Q10, Q11, Q12, Q13, Q14, Q15]), "depth" : 0.2 * mm, "offsetDistance" : 25 * mm, "hasSecondDirection" : true, "secondDirectionOppositeDirection" : true, "secondDirectionDepth" : 1 * mm});
        }
        {
            var Q0;
            Q0=makeQuery(id+"F2.imprint","IMPRINT",FACE,{"disambiguationData":[TD([[makeQuery(id+"F2.imprint","IMPRINT",EDGE,{"derivedFrom":sQuery(id+"F2.wireOp",EDGE,"E61.MirrorCS")}),1.0]])]});
            var Q1;
            Q1=makeQuery(id+"F2.imprint","IMPRINT",FACE,{"disambiguationData":[TD([[makeQuery(id+"F2.imprint","IMPRINT",EDGE,{"derivedFrom":sQuery(id+"F2.wireOp",EDGE,"E62.MirrorCS")}),1.0]])]});
            var Q2;
            {var subQ0=sQuery(id+"F2.wireOp",EDGE,"E60");Q2=makeQuery(id+"F2.imprint","IMPRINT",FACE,{"disambiguationData":[TD([[makeQuery(id+"F2.imprint","IMPRINT",EDGE,{"derivedFrom":subQ0}),-1.0]])]});}
            var Q3;
            {var subQ0=sQuery(id+"F2.wireOp",EDGE,"E60");Q3=makeQuery(id+"F2.imprint","IMPRINT",FACE,{"disambiguationData":[TD([[makeQuery(id+"F2.imprint","IMPRINT",EDGE,{"derivedFrom":subQ0}),1.0]])]});}
            var Q4;
            {var subQ0=sQuery(id+"F2.wireOp",EDGE,"E61.MirrorCS");Q4=makeQuery(id+"F2.imprint","IMPRINT",FACE,{"disambiguationData":[TD([[makeQuery(id+"F2.imprint","IMPRINT",EDGE,{"derivedFrom":subQ0}),-1.0]])]});}
            var Q5;
            {var subQ0=sQuery(id+"F2.wireOp",EDGE,"E63.MirrorCS");Q5=makeQuery(id+"F2.imprint","IMPRINT",FACE,{"disambiguationData":[TD([[makeQuery(id+"F2.imprint","IMPRINT",EDGE,{"derivedFrom":subQ0}),1.0]])]});}
            extrude(context, id + "F9", {"entities" : qUnion([Q0, Q1, Q2, Q3, Q4, Q5]), "oppositeDirection" : true, "depth" : 1 * mm, "offsetDistance" : 25 * mm});
        }
        {
            var Q0;
            Q0=makeQuery(id+"F3.opExtrude","CAP_FACE",FACE,{"disambiguationData":[OSD([sQuery(id+"F0.wireOp",EDGE,"E7"),sQuery(id+"F0.wireOp",EDGE,"E8.MirrorCS"),sQuery(id+"F0.wireOp",EDGE,"E9.MirrorCS"),sQuery(id+"F0.wireOp",EDGE,"E10.MirrorCS")])],"isStart":false});
            chamfer(context, id + "F10", {"entities" : qUnion([Q0]), "chamferType" : ChamferType.OFFSET_ANGLE, "width" : 2.98 * mm, "oppositeDirection" : false, "angle" : 18 * degree});
        }
        {
            var Q0;
            Q0=makeQuery(id+"F4.opExtrude","CAP_EDGE",EDGE,{"disambiguationData":[OSD([sQuery(id+"F0.wireOp",EDGE,"E3")])],"isStart":false});
            var Q1;
            Q1=makeQuery(id+"F4.opExtrude","CAP_EDGE",EDGE,{"disambiguationData":[OSD([sQuery(id+"F0.wireOp",EDGE,"E4.MirrorCS")])],"isStart":false});
            chamfer(context, id + "F11", {"entities" : qUnion([Q0, Q1]), "chamferType" : ChamferType.OFFSET_ANGLE, "width" : 1.1 * mm, "oppositeDirection" : false, "angle" : 66 * degree, "tangentPropagation" : true});
        }
        {
            var Q0;
            Q0=makeQuery(id+"F4.opExtrude","CAP_EDGE",EDGE,{"disambiguationData":[OSD([sQuery(id+"F0.wireOp",EDGE,"E5.MirrorCS")])],"isStart":false});
            var Q1;
            Q1=makeQuery(id+"F4.opExtrude","CAP_EDGE",EDGE,{"disambiguationData":[OSD([sQuery(id+"F0.wireOp",EDGE,"E6.MirrorCS")])],"isStart":false});
            chamfer(context, id + "F12", {"entities" : qUnion([Q0, Q1]), "chamferType" : ChamferType.OFFSET_ANGLE, "width" : 1.1 * mm, "oppositeDirection" : true, "angle" : 66 * degree, "tangentPropagation" : true});
        }
        {
            var Q0;
            Q0=makeQuery(id+"F5.opExtrude","CAP_FACE",FACE,{"disambiguationData":[OSD([sQuery(id+"F0.wireOp",EDGE,"E11"),sQuery(id+"F0.wireOp",EDGE,"E12.MirrorCS"),sQuery(id+"F0.wireOp",EDGE,"E13.MirrorCS"),sQuery(id+"F0.wireOp",EDGE,"E14.MirrorCS"),sQuery(id+"F0.wireOp",EDGE,"E15.MirrorCS"),sQuery(id+"F0.wireOp",EDGE,"E16.MirrorCS"),sQuery(id+"F0.wireOp",EDGE,"E17.MirrorCS"),sQuery(id+"F0.wireOp",EDGE,"E18.MirrorCS")])],"isStart":false});
            chamfer(context, id + "F13", {"entities" : qUnion([Q0]), "chamferType" : ChamferType.OFFSET_ANGLE, "width" : 1 * mm, "oppositeDirection" : true, "angle" : 63 * degree});
        }
        {
            var Q0;
            Q0=makeQuery(id+"F6.opExtrude","CAP_EDGE",EDGE,{"disambiguationData":[OSD([sQuery(id+"F0.wireOp",EDGE,"E23")])],"isStart":false});
            var Q1;
            Q1=makeQuery(id+"F6.opExtrude","CAP_EDGE",EDGE,{"disambiguationData":[OSD([sQuery(id+"F0.wireOp",EDGE,"E24.MirrorCS")])],"isStart":false});
            var Q2;
            Q2=makeQuery(id+"F6.opExtrude","CAP_EDGE",EDGE,{"disambiguationData":[OSD([sQuery(id+"F0.wireOp",EDGE,"E26.MirrorCS")])],"isStart":false});
            var Q3;
            Q3=makeQuery(id+"F6.opExtrude","CAP_EDGE",EDGE,{"disambiguationData":[OSD([sQuery(id+"F0.wireOp",EDGE,"E25.MirrorCS")])],"isStart":false});
            chamfer(context, id + "F14", {"entities" : qUnion([Q0, Q1, Q2, Q3]), "chamferType" : ChamferType.OFFSET_ANGLE, "width" : 1.7 * mm, "oppositeDirection" : true, "angle" : 61.2 * degree, "tangentPropagation" : true});
        }
        {
            var Q0;
            Q0=makeQuery(id+"F8.opExtrude","CAP_EDGE",EDGE,{"disambiguationData":[OSD([sQuery(id+"F1.wireOp",EDGE,"E50")])],"isStart":false});
            var Q1;
            Q1=makeQuery(id+"F8.opExtrude","CAP_EDGE",EDGE,{"disambiguationData":[OSD([sQuery(id+"F1.wireOp",EDGE,"E51.MirrorCS")])],"isStart":false});
            var Q2;
            Q2=makeQuery(id+"F8.opExtrude","CAP_EDGE",EDGE,{"disambiguationData":[OSD([sQuery(id+"F1.wireOp",EDGE,"E52.MirrorCS")])],"isStart":false});
            var Q3;
            Q3=makeQuery(id+"F8.opExtrude","CAP_EDGE",EDGE,{"disambiguationData":[OSD([sQuery(id+"F1.wireOp",EDGE,"E53.MirrorCS")])],"isStart":false});
            var Q4;
            Q4=makeQuery(id+"F8.opExtrude","CAP_EDGE",EDGE,{"disambiguationData":[OSD([sQuery(id+"F1.wireOp",EDGE,"E57.MirrorCS")])],"isStart":false});
            var Q5;
            Q5=makeQuery(id+"F8.opExtrude","CAP_EDGE",EDGE,{"disambiguationData":[OSD([sQuery(id+"F1.wireOp",EDGE,"E56.MirrorCS")])],"isStart":false});
            var Q6;
            Q6=makeQuery(id+"F8.opExtrude","CAP_EDGE",EDGE,{"disambiguationData":[OSD([sQuery(id+"F1.wireOp",EDGE,"E54.MirrorCS")])],"isStart":false});
            var Q7;
            Q7=makeQuery(id+"F8.opExtrude","CAP_EDGE",EDGE,{"disambiguationData":[OSD([sQuery(id+"F1.wireOp",EDGE,"E55.MirrorCS")])],"isStart":false});
            chamfer(context, id + "F15", {"entities" : qUnion([Q0, Q1, Q2, Q3, Q4, Q5, Q6, Q7]), "width" : 1 * mm, "tangentPropagation" : true});
        }
        {
            var Q0;
            Q0=makeQuery(id+"F7.opExtrude","CAP_FACE",FACE,{"disambiguationData":[OSD([sQuery(id+"F1.wireOp",EDGE,"E38"),sQuery(id+"F1.wireOp",EDGE,"E39"),sQuery(id+"F1.wireOp",EDGE,"E40.MirrorCS"),sQuery(id+"F1.wireOp",EDGE,"E41.MirrorCS"),sQuery(id+"F1.wireOp",EDGE,"E42.MirrorCS"),sQuery(id+"F1.wireOp",EDGE,"E43.MirrorCS"),sQuery(id+"F1.wireOp",EDGE,"E44.MirrorCS"),sQuery(id+"F1.wireOp",EDGE,"E45.MirrorCS")])],"isStart":false});
            chamfer(context, id + "F16", {"entities" : qUnion([Q0]), "width" : 1 * mm, "tangentPropagation" : true});
        }
        {
            var Q0;
            Q0=makeQuery(id+"F9.opExtrude","CAP_FACE",FACE,{"disambiguationData":[OSD([sQuery(id+"F2.wireOp",EDGE,"E64"),sQuery(id+"F2.wireOp",EDGE,"E65"),sQuery(id+"F2.wireOp",EDGE,"E70"),sQuery(id+"F2.wireOp",EDGE,"E71"),sQuery(id+"F2.wireOp",EDGE,"E72"),sQuery(id+"F2.wireOp",EDGE,"E73"),sQuery(id+"F2.wireOp",EDGE,"E74"),sQuery(id+"F2.wireOp",EDGE,"E75")])],"isStart":true});
            chamfer(context, id + "F17", {"entities" : qUnion([Q0]), "chamferType" : ChamferType.OFFSET_ANGLE, "width" : 2.1 * mm, "oppositeDirection" : false, "angle" : 20 * degree, "tangentPropagation" : true});
        }
    });
